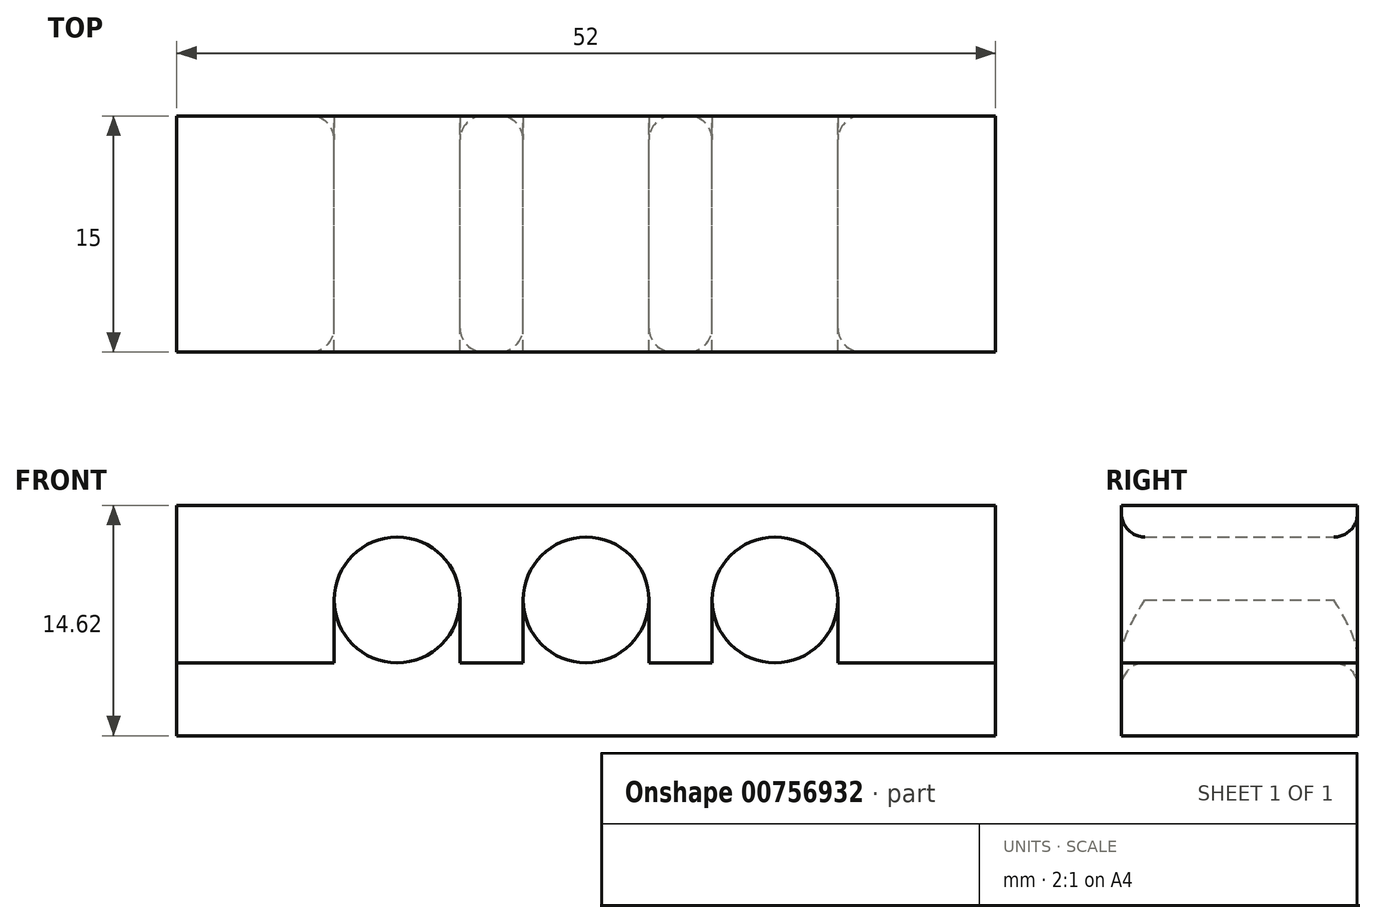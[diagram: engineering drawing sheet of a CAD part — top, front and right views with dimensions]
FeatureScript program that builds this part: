
annotation { "Feature Type Name" : "Feature", "Feature Type Description" : "" }
export const myFeature = defineFeature(function(context is Context, id is Id, definition is map)
    precondition{}
    {
        {
            var Q0;
            Q0=qCreatedBy(makeId("Front.planeOp"),FACE);
            var sketch = newSketch(context, id + "F0", { "sketchPlane" : qUnion([Q0])});
            skCircle(sketch, "E0", {"center": v(0, 0) * mm, "radius": 4 * mm});
            skCircle(sketch, "E1", {"center": v(12, 0) * mm, "radius": 4 * mm});
            skCircle(sketch, "E2", {"center": v(-12, 0) * mm, "radius": 4 * mm});
            skLineSegment(sketch, "E3.bottom", {"start": v(-26, 6) * mm, "end": v(26, 6) * mm});
            skLineSegment(sketch, "E3.top", {"start": v(-26, -4) * mm, "end": v(26, -4) * mm});
            skLineSegment(sketch, "E3.left", {"start": v(-26, 6) * mm, "end": v(-26, -4) * mm});
            skLineSegment(sketch, "E3.right", {"start": v(26, 6) * mm, "end": v(26, -4) * mm});
            skLineSegment(sketch, "E4", {"start": v(16, 0) * mm, "end": v(16, -4) * mm});
            skLineSegment(sketch, "E5", {"start": v(8, 0) * mm, "end": v(8, -4) * mm});
            skLineSegment(sketch, "E6", {"start": v(4, 0) * mm, "end": v(4, -4) * mm});
            skLineSegment(sketch, "E7", {"start": v(-4, 0) * mm, "end": v(-4, -4) * mm});
            skLineSegment(sketch, "E8", {"start": v(-8, 0) * mm, "end": v(-8, -4) * mm});
            skLineSegment(sketch, "E9", {"start": v(-16, 0) * mm, "end": v(-16, -4) * mm});
            skPoint(sketch, "E10", {"position": v(-21, 6) * mm});
            skPoint(sketch, "E11", {"position": v(21, 6) * mm});
            skPoint(sketch, "E12.start.orphan", {"position": v(-21, -4) * mm});
            skPoint(sketch, "E13.start.orphan", {"position": v(21, -4) * mm});
            skLineSegment(sketch, "E14.bottom", {"start": v(26, -4) * mm, "end": v(-26, -4) * mm});
            skLineSegment(sketch, "E14.top", {"start": v(26, -8.62) * mm, "end": v(-26, -8.62) * mm});
            skLineSegment(sketch, "E14.left", {"start": v(26, -4) * mm, "end": v(26, -8.62) * mm});
            skLineSegment(sketch, "E14.right", {"start": v(-26, -4) * mm, "end": v(-26, -8.62) * mm});
            skSolve(sketch);
        }
        {
            var Q0;
            Q0=makeQuery(id+"F0.imprint","IMPRINT",FACE,{"disambiguationData":[TD([[makeQuery(id+"F0.imprint","IMPRINT",EDGE,{"derivedFrom":sQuery(id+"F0.wireOp",EDGE,"E3.bottom")}),-1.0]])]});
            var Q1;
            {var subQ0=sQuery(id+"F0.wireOp",EDGE,"E4");Q1=makeQuery(id+"F0.imprint","IMPRINT",FACE,{"disambiguationData":[TD([[makeQuery(id+"F0.imprint","IMPRINT",EDGE,{"derivedFrom":subQ0}),1.0]])]});}
            extrude(context, id + "F1", {"entities" : qUnion([Q0, Q1]), "endBound" : BoundingType.SYMMETRIC, "depth" : 15 * mm, "offsetDistance" : 25 * mm});
        }
        {
            var Q0;
            Q0=makeQuery(id+"F1.opExtrude","CAP_EDGE",EDGE,{"disambiguationData":[OSD([sQuery(id+"F0.wireOp",EDGE,"E2")])],"isStart":true});
            var Q1;
            Q1=makeQuery(id+"F1.opExtrude","CAP_EDGE",EDGE,{"disambiguationData":[OSD([sQuery(id+"F0.wireOp",EDGE,"E0")])],"isStart":true});
            var Q2;
            Q2=makeQuery(id+"F1.opExtrude","CAP_EDGE",EDGE,{"disambiguationData":[OSD([sQuery(id+"F0.wireOp",EDGE,"E1")])],"isStart":true});
            var Q3;
            Q3=makeQuery(id+"F1.opExtrude","CAP_EDGE",EDGE,{"disambiguationData":[OSD([sQuery(id+"F0.wireOp",EDGE,"E2")])],"isStart":false});
            var Q4;
            Q4=makeQuery(id+"F1.opExtrude","CAP_EDGE",EDGE,{"disambiguationData":[OSD([sQuery(id+"F0.wireOp",EDGE,"E0")])],"isStart":false});
            var Q5;
            Q5=makeQuery(id+"F1.opExtrude","CAP_EDGE",EDGE,{"disambiguationData":[OSD([sQuery(id+"F0.wireOp",EDGE,"E1")])],"isStart":false});
            fillet(context, id + "F2", {"entities" : qUnion([Q0, Q1, Q2, Q3, Q4, Q5]), "radius" : 1.5 * mm, "tangentPropagation" : true, "allowEdgeOverflow" : false});
        }
        {
            var Q0;
            {var subQ0=sQuery(id+"F0.wireOp",EDGE,"E5");Q0=makeQuery(id+"F0.imprint","IMPRINT",FACE,{"disambiguationData":[TD([[makeQuery(id+"F0.imprint","IMPRINT",EDGE,{"derivedFrom":subQ0}),1.0]])]});}
            var Q1;
            {var subQ0=sQuery(id+"F0.wireOp",EDGE,"E7");Q1=makeQuery(id+"F0.imprint","IMPRINT",FACE,{"disambiguationData":[TD([[makeQuery(id+"F0.imprint","IMPRINT",EDGE,{"derivedFrom":subQ0}),1.0]])]});}
            var Q2;
            {var subQ0=sQuery(id+"F0.wireOp",EDGE,"E4");Q2=makeQuery(id+"F0.imprint","IMPRINT",FACE,{"disambiguationData":[TD([[makeQuery(id+"F0.imprint","IMPRINT",EDGE,{"derivedFrom":subQ0}),-1.0]])]});}
            var Q3;
            {var subQ0=sQuery(id+"F0.wireOp",EDGE,"E9");Q3=makeQuery(id+"F0.imprint","IMPRINT",FACE,{"disambiguationData":[TD([[makeQuery(id+"F0.imprint","IMPRINT",EDGE,{"derivedFrom":subQ0}),1.0]])]});}
            var Q4;
            {var subQ0=sQuery(id+"F0.wireOp",EDGE,"E6");Q4=makeQuery(id+"F0.imprint","IMPRINT",FACE,{"disambiguationData":[TD([[makeQuery(id+"F0.imprint","IMPRINT",EDGE,{"derivedFrom":subQ0}),-1.0]])]});}
            var Q5;
            Q5=makeQuery(id+"F0.imprint","IMPRINT",FACE,{"disambiguationData":[TD([[makeQuery(id+"F0.imprint","IMPRINT",EDGE,{"derivedFrom":sQuery(id+"F0.wireOp",EDGE,"E14.top")}),-1.0]])]});
            var Q6;
            {var subQ0=sQuery(id+"F0.wireOp",EDGE,"E8");Q6=makeQuery(id+"F0.imprint","IMPRINT",FACE,{"disambiguationData":[TD([[makeQuery(id+"F0.imprint","IMPRINT",EDGE,{"derivedFrom":subQ0}),-1.0]])]});}
            extrude(context, id + "F3", {"entities" : qUnion([Q0, Q1, Q2, Q3, Q4, Q5, Q6]), "endBound" : BoundingType.SYMMETRIC, "depth" : 15 * mm, "offsetDistance" : 25 * mm});
        }
        {
            var Q0;
            Q0=makeQuery(id+"F3.opExtrude","CAP_EDGE",EDGE,{"disambiguationData":[OSD([sQuery(id+"F0.wireOp",EDGE,"E0")])],"isStart":true});
            var Q1;
            Q1=makeQuery(id+"F3.opExtrude","CAP_EDGE",EDGE,{"disambiguationData":[OSD([sQuery(id+"F0.wireOp",EDGE,"E1")])],"isStart":false});
            var Q2;
            Q2=makeQuery(id+"F3.opExtrude","CAP_EDGE",EDGE,{"disambiguationData":[OSD([sQuery(id+"F0.wireOp",EDGE,"E1")])],"isStart":true});
            var Q3;
            Q3=makeQuery(id+"F3.opExtrude","CAP_EDGE",EDGE,{"disambiguationData":[OSD([sQuery(id+"F0.wireOp",EDGE,"E0")])],"isStart":false});
            var Q4;
            Q4=makeQuery(id+"F3.opExtrude","CAP_EDGE",EDGE,{"disambiguationData":[OSD([sQuery(id+"F0.wireOp",EDGE,"E2")])],"isStart":false});
            var Q5;
            Q5=makeQuery(id+"F3.opExtrude","CAP_EDGE",EDGE,{"disambiguationData":[OSD([sQuery(id+"F0.wireOp",EDGE,"E2")])],"isStart":true});
            fillet(context, id + "F4", {"entities" : qUnion([Q0, Q1, Q2, Q3, Q4, Q5]), "radius" : 1.5 * mm, "tangentPropagation" : true, "allowEdgeOverflow" : false});
        }
    });
